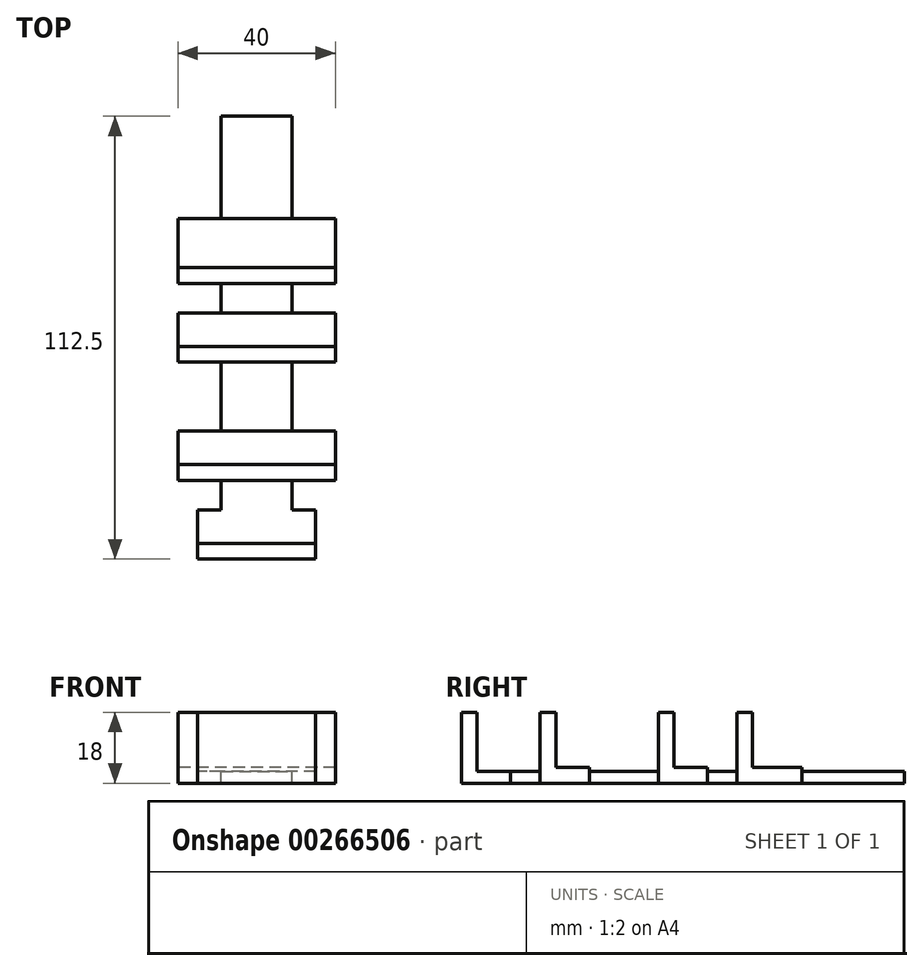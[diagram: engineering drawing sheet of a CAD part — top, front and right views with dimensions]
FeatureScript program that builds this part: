
annotation { "Feature Type Name" : "Feature", "Feature Type Description" : "" }
export const myFeature = defineFeature(function(context is Context, id is Id, definition is map)
    precondition{}
    {
        {
            var Q0;
            Q0=qCreatedBy(makeId("Front.planeOp"),FACE);
            var sketch = newSketch(context, id + "F0", { "sketchPlane" : qUnion([Q0])});
            skLineSegment(sketch, "E0.bottom", {"start": v(-14.72, 15.54) * mm, "end": v(15.28, 15.54) * mm});
            skLineSegment(sketch, "E0.top", {"start": v(-14.72, -2.46) * mm, "end": v(15.28, -2.46) * mm});
            skLineSegment(sketch, "E0.left", {"start": v(-14.72, 15.54) * mm, "end": v(-14.72, -2.46) * mm});
            skLineSegment(sketch, "E0.right", {"start": v(15.28, 15.54) * mm, "end": v(15.28, -2.46) * mm});
            skSolve(sketch);
        }
        {
            var Q0;
            Q0=makeQuery(id+"F0.imprint","IMPRINT",FACE,{"disambiguationData":[TD([[makeQuery(id+"F0.imprint","IMPRINT",EDGE,{"derivedFrom":sQuery(id+"F0.wireOp",EDGE,"E0.bottom")}),-1.0]])]});
            extrude(context, id + "F1", {"entities" : qUnion([Q0]), "oppositeDirection" : true, "depth" : 4 * mm});
        }
        {
            var Q0;
            Q0=makeQuery(id+"F1.opExtrude","CAP_FACE",FACE,{"disambiguationData":[OSD([sQuery(id+"F0.wireOp",EDGE,"E0.bottom"),sQuery(id+"F0.wireOp",EDGE,"E0.top"),sQuery(id+"F0.wireOp",EDGE,"E0.left"),sQuery(id+"F0.wireOp",EDGE,"E0.right")])],"isStart":false});
            var sketch = newSketch(context, id + "F2", { "sketchPlane" : qUnion([Q0])});
            skLineSegment(sketch, "E1.bottom", {"start": v(-15.28, -2.46) * mm, "end": v(14.72, -2.46) * mm});
            skLineSegment(sketch, "E1.top", {"start": v(-15.28, 0.54) * mm, "end": v(14.72, 0.54) * mm});
            skLineSegment(sketch, "E1.left", {"start": v(-15.28, -2.46) * mm, "end": v(-15.28, 0.54) * mm});
            skLineSegment(sketch, "E1.right", {"start": v(14.72, -2.46) * mm, "end": v(14.72, 0.54) * mm});
            skSolve(sketch);
        }
        {
            var Q0;
            Q0=makeQuery(id+"F2.imprint","IMPRINT",FACE,{"disambiguationData":[TD([[makeQuery(id+"F2.imprint","IMPRINT",EDGE,{"derivedFrom":sQuery(id+"F2.wireOp",EDGE,"E1.bottom")}),-1.0]])]});
            extrude(context, id + "F3", {"entities" : qUnion([Q0]), "operationType" : NewBodyOperationType.ADD, "depth" : 8.5 * mm});
        }
        {
            var Q0;
            Q0=makeQuery(id+"F3.opExtrude","CAP_FACE",FACE,{"disambiguationData":[OSD([sQuery(id+"F2.wireOp",EDGE,"E1.bottom"),sQuery(id+"F2.wireOp",EDGE,"E1.top"),sQuery(id+"F2.wireOp",EDGE,"E1.left"),sQuery(id+"F2.wireOp",EDGE,"E1.right")])],"isStart":false});
            var sketch = newSketch(context, id + "F4", { "sketchPlane" : qUnion([Q0])});
            skLineSegment(sketch, "E2.bottom", {"start": v(-9.28, 0.54) * mm, "end": v(8.72, 0.54) * mm});
            skLineSegment(sketch, "E2.top", {"start": v(-9.28, -2.46) * mm, "end": v(8.72, -2.46) * mm});
            skLineSegment(sketch, "E2.left", {"start": v(-9.28, 0.54) * mm, "end": v(-9.28, -2.46) * mm});
            skLineSegment(sketch, "E2.right", {"start": v(8.72, 0.54) * mm, "end": v(8.72, -2.46) * mm});
            skSolve(sketch);
        }
        {
            var Q0;
            Q0=makeQuery(id+"F4.imprint","IMPRINT",FACE,{"disambiguationData":[TD([[makeQuery(id+"F4.imprint","IMPRINT",EDGE,{"derivedFrom":sQuery(id+"F4.wireOp",EDGE,"E2.bottom")}),-1.0]])]});
            extrude(context, id + "F5", {"entities" : qUnion([Q0]), "operationType" : NewBodyOperationType.ADD, "depth" : 100 * mm});
        }
        {
            var Q0;
            Q0=makeQuery(id+"F1.opExtrude","CAP_FACE",FACE,{"disambiguationData":[OSD([sQuery(id+"F0.wireOp",EDGE,"E0.bottom"),sQuery(id+"F0.wireOp",EDGE,"E0.top"),sQuery(id+"F0.wireOp",EDGE,"E0.left"),sQuery(id+"F0.wireOp",EDGE,"E0.right")])],"isStart":true});
            var sketch = newSketch(context, id + "F6", { "sketchPlane" : qUnion([Q0])});
            skLineSegment(sketch, "E3.bottom", {"start": v(-19.72, 15.54) * mm, "end": v(20.28, 15.54) * mm});
            skLineSegment(sketch, "E3.top", {"start": v(-19.72, -2.46) * mm, "end": v(20.28, -2.46) * mm});
            skLineSegment(sketch, "E3.left", {"start": v(-19.72, 15.54) * mm, "end": v(-19.72, -2.46) * mm});
            skLineSegment(sketch, "E3.right", {"start": v(20.28, 15.54) * mm, "end": v(20.28, -2.46) * mm});
            skSolve(sketch);
        }
        {
            var Q0;
            Q0=makeQuery(id+"F6.imprint","IMPRINT",FACE,{"disambiguationData":[TD([[makeQuery(id+"F6.imprint","IMPRINT",EDGE,{"derivedFrom":sQuery(id+"F6.wireOp",EDGE,"E3.bottom")}),-1.0]])]});
            extrude(context, id + "F7", {"entities" : qUnion([Q0]), "oppositeDirection" : true, "depth" : 24 * mm, "hasSecondDirection" : true, "secondDirectionOppositeDirection" : true, "secondDirectionDepth" : 20 * mm});
        }
        {
            var Q0;
            Q0 = qSketchRegion(id + "F6", true);
            extrude(context, id + "F8", {"entities" : qUnion([Q0]), "oppositeDirection" : true, "depth" : 54 * mm, "hasSecondDirection" : true, "secondDirectionOppositeDirection" : true, "secondDirectionDepth" : 50 * mm});
        }
        {
            var Q0;
            Q0 = qSketchRegion(id + "F6", true);
            extrude(context, id + "F9", {"entities" : qUnion([Q0]), "oppositeDirection" : true, "depth" : 74 * mm, "hasSecondDirection" : true, "secondDirectionOppositeDirection" : true, "secondDirectionDepth" : 70 * mm});
        }
        {
            var Q0;
            Q0=makeQuery(id+"F7.opExtrude","CAP_FACE",FACE,{"disambiguationData":[OSD([sQuery(id+"F6.wireOp",EDGE,"E3.bottom"),sQuery(id+"F6.wireOp",EDGE,"E3.top"),sQuery(id+"F6.wireOp",EDGE,"E3.left"),sQuery(id+"F6.wireOp",EDGE,"E3.right")])],"isStart":false});
            var sketch = newSketch(context, id + "F10", { "sketchPlane" : qUnion([Q0])});
            skLineSegment(sketch, "E4.bottom", {"start": v(-20.28, -2.46) * mm, "end": v(19.72, -2.46) * mm});
            skLineSegment(sketch, "E4.top", {"start": v(-20.28, 1.54) * mm, "end": v(19.72, 1.54) * mm});
            skLineSegment(sketch, "E4.left", {"start": v(-20.28, -2.46) * mm, "end": v(-20.28, 1.54) * mm});
            skLineSegment(sketch, "E4.right", {"start": v(19.72, -2.46) * mm, "end": v(19.72, 1.54) * mm});
            skSolve(sketch);
        }
        {
            var Q0;
            Q0=makeQuery(id+"F10.imprint","IMPRINT",FACE,{"disambiguationData":[TD([[makeQuery(id+"F10.imprint","IMPRINT",EDGE,{"derivedFrom":sQuery(id+"F10.wireOp",EDGE,"E4.bottom")}),-1.0]])]});
            extrude(context, id + "F11", {"entities" : qUnion([Q0]), "operationType" : NewBodyOperationType.ADD, "depth" : 8.5 * mm});
        }
        {
            var Q0;
            Q0=makeQuery(id+"F8.opExtrude","CAP_FACE",FACE,{"disambiguationData":[OSD([sQuery(id+"F6.wireOp",EDGE,"E3.bottom"),sQuery(id+"F6.wireOp",EDGE,"E3.top"),sQuery(id+"F6.wireOp",EDGE,"E3.left"),sQuery(id+"F6.wireOp",EDGE,"E3.right")])],"isStart":false});
            var sketch = newSketch(context, id + "F12", { "sketchPlane" : qUnion([Q0])});
            skLineSegment(sketch, "E5.bottom", {"start": v(-20.28, -2.46) * mm, "end": v(19.72, -2.46) * mm});
            skLineSegment(sketch, "E5.top", {"start": v(-20.28, 1.54) * mm, "end": v(19.72, 1.54) * mm});
            skLineSegment(sketch, "E5.left", {"start": v(-20.28, -2.46) * mm, "end": v(-20.28, 1.54) * mm});
            skLineSegment(sketch, "E5.right", {"start": v(19.72, -2.46) * mm, "end": v(19.72, 1.54) * mm});
            skSolve(sketch);
        }
        {
            var Q0;
            Q0=makeQuery(id+"F12.imprint","IMPRINT",FACE,{"disambiguationData":[TD([[makeQuery(id+"F12.imprint","IMPRINT",EDGE,{"derivedFrom":sQuery(id+"F12.wireOp",EDGE,"E5.bottom")}),-1.0]])]});
            extrude(context, id + "F13", {"entities" : qUnion([Q0]), "operationType" : NewBodyOperationType.ADD, "depth" : 8.5 * mm});
        }
        {
            var Q0;
            Q0=makeQuery(id+"F9.opExtrude","CAP_FACE",FACE,{"disambiguationData":[OSD([sQuery(id+"F6.wireOp",EDGE,"E3.bottom"),sQuery(id+"F6.wireOp",EDGE,"E3.top"),sQuery(id+"F6.wireOp",EDGE,"E3.left"),sQuery(id+"F6.wireOp",EDGE,"E3.right")])],"isStart":false});
            var sketch = newSketch(context, id + "F14", { "sketchPlane" : qUnion([Q0])});
            skLineSegment(sketch, "E6.bottom", {"start": v(-20.28, -2.46) * mm, "end": v(19.72, -2.46) * mm});
            skLineSegment(sketch, "E6.top", {"start": v(-20.28, 1.54) * mm, "end": v(19.72, 1.54) * mm});
            skLineSegment(sketch, "E6.left", {"start": v(-20.28, -2.46) * mm, "end": v(-20.28, 1.54) * mm});
            skLineSegment(sketch, "E6.right", {"start": v(19.72, -2.46) * mm, "end": v(19.72, 1.54) * mm});
            skSolve(sketch);
        }
        {
            var Q0;
            Q0=makeQuery(id+"F14.imprint","IMPRINT",FACE,{"disambiguationData":[TD([[makeQuery(id+"F14.imprint","IMPRINT",EDGE,{"derivedFrom":sQuery(id+"F14.wireOp",EDGE,"E6.top")}),-1.0]])]});
            extrude(context, id + "F15", {"entities" : qUnion([Q0]), "operationType" : NewBodyOperationType.ADD, "depth" : 12.5 * mm});
        }
    });
